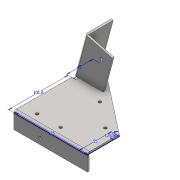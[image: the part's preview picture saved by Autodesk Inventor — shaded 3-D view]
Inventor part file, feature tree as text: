
AUTODESK INVENTOR PART (.ipt)
format: ipt  version: 2016 (Build 200138000, 138)  size: 269,824 bytes
history: native  units: mm
features: sheet_metal_op x7, hole x6, other x5, sketch x4, plane x3
ambient origin geometry x8: Origin, YZ Plane, XZ Plane, XY Plane, X Axis, Y Axis, Z Axis, Center Point
bodies: Solid1 (feature_tree)
feature tree (25):
  sketch  "Sketch1"  dims[d0=125.0mm d1=101.6mm]
  plane  "Work Plane1"
  sheet_metal_op  "Face1"
  sheet_metal_op  "Face4"
  plane  "Work Plane3"
  sheet_metal_op  "Face5"
  plane  "Work Plane4"
  sheet_metal_op  "Face6"
  hole  "Hole2"  [1 undecoded]
  hole  "Hole3"  [1 undecoded]
  hole  "Hole4"  [1 undecoded]
  hole  "Hole5"  [1 undecoded]
  hole  "Hole6"  [1 undecoded]
  hole  "Hole7"  [1 undecoded]
  other  "Plate1"
  sketch  "Sketch4"  dims[d3=55.0mm d4=22.340214mm]
  other  "Plate4"
  sheet_metal_op  "Bend3"
  other  "Plate5"
  sheet_metal_op  "Bend4"
  sketch  "Sketch7"  dims[d13=3.0mm d24=25.0mm]
  other  "Plate6"
  sheet_metal_op  "Bend5"
  sketch  "Sketch8"  dims[d25=25.0mm d26=1.5mm d27=3.0mm d28=1.5mm d29=6.0mm d30=3.0mm d31=165.0deg d34=1.5mm d35=3.0mm d36=1.5mm d37=6.0mm d38=3.0mm d43=0.5mm d44=3.0mm d45=1.5mm d46=6.0mm d47=3.0mm d57=15.0mm d58=15.0mm d59=5.0mm d60=6.0mm d61=4.0mm d62=2.0mm d63=90.0deg d64=3.0mm d65=20.594885mm d66=50.0mm d131=15.0mm d68=5.0mm d69=6.0mm d70=4.0mm d71=2.0mm d72=90.0deg d73=3.0mm d74=20.594885mm d76=15.0mm d77=5.0mm d78=15.0mm d79=5.0mm d80=55.0mm d81=5.0mm d82=6.0mm d83=4.0mm d84=2.0mm d85=90.0deg d86=3.0mm d87=20.594885mm d88=60.0mm d89=15.0mm d90=5.0mm d91=6.0mm d92=4.0mm d93=2.0mm d94=90.0deg d95=3.0mm d96=20.594885mm d97=100.0mm d107=15.0mm d99=5.0mm d100=6.0mm d101=4.0mm d102=2.0mm d103=90.0deg d104=3.0mm d105=20.594885mm d109=10.0mm d110=45.0mm d111=5.0mm d112=6.0mm d113=4.0mm d114=2.0mm d115=90.0deg d116=3.0mm d117=20.594885mm d118=45.0mm d119=78.0mm d120=45.0mm d121=90.0deg d123=90.0deg d124=90.0deg d127=45.0mm d128=90.0deg d129=90.0deg]
  other  "Definition1"
note: 6 required parameter values undecoded (feature->parameter linkage not recoverable at this tier; creation-order binding heuristic only, values carry confidence <= 0.55)
